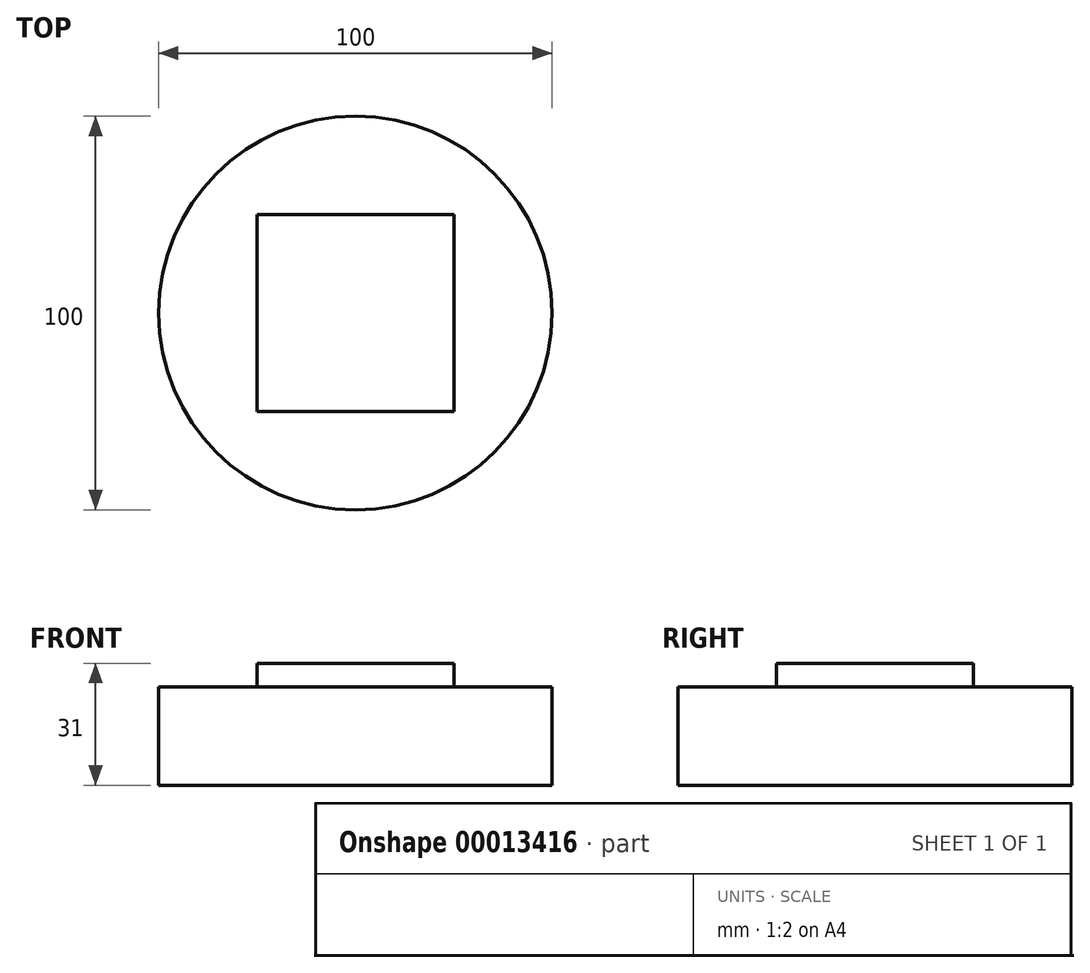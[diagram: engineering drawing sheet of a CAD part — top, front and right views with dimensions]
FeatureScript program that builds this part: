
annotation { "Feature Type Name" : "Feature", "Feature Type Description" : "" }
export const myFeature = defineFeature(function(context is Context, id is Id, definition is map)
    precondition{}
    {
        {
            var Q0;
            Q0=qCreatedBy(makeId("Top.planeOp"),FACE);
            var sketch = newSketch(context, id + "F0", { "sketchPlane" : qUnion([Q0])});
            skLineSegment(sketch, "E0.rect.bottom", {"start": v(25, -25) * mm, "end": v(-25, -25) * mm});
            skLineSegment(sketch, "E0.rect.top", {"start": v(25, 25) * mm, "end": v(-25, 25) * mm});
            skLineSegment(sketch, "E0.rect.left", {"start": v(25, -25) * mm, "end": v(25, 25) * mm});
            skLineSegment(sketch, "E0.rect.right", {"start": v(-25, -25) * mm, "end": v(-25, 25) * mm});
            skPoint(sketch, "E0.rect.middle", {"position": v(0, 0) * mm});
            skSolve(sketch);
        }
        {
            var Q0;
            Q0 = qSketchRegion(id + "F0", true);
            extrude(context, id + "F1", {"entities" : qUnion([Q0]), "oppositeDirection" : true, "depth" : 6 * mm});
        }
        {
            var Q0;
            Q0=makeQuery(id+"F1.opExtrude","CAP_FACE",FACE,{"disambiguationData":[OSD([sQuery(id+"F0.wireOp",EDGE,"E0.rect.bottom"),sQuery(id+"F0.wireOp",EDGE,"E0.rect.top"),sQuery(id+"F0.wireOp",EDGE,"E0.rect.left"),sQuery(id+"F0.wireOp",EDGE,"E0.rect.right")])],"isStart":false});
            var sketch = newSketch(context, id + "F2", { "sketchPlane" : qUnion([Q0])});
            skCircle(sketch, "E1", {"center": v(0, 0) * mm, "radius": 50 * mm});
            skSolve(sketch);
        }
        {
            var Q0;
            Q0 = qSketchRegion(id + "F2", true);
            extrude(context, id + "F3", {"entities" : qUnion([Q0]), "depth" : 25 * mm});
        }
    });
